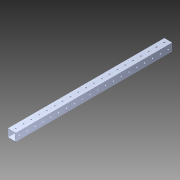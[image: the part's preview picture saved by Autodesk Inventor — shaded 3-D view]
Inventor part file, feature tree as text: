
AUTODESK INVENTOR PART (.ipt)
format: ipt  version: 2014 SP1 (Build 180222100, 222)  size: 1,191,936 bytes
history: native  units: in
note: dims shown in document units (in); Inventor stores cm internally (conversion verified against a paired STEP export)
features: pattern_circular x1, other x1, extrude x1, imported_body x1, sketch x1
ambient origin geometry x8: Origin, YZ Plane, XZ Plane, XY Plane, X Axis, Y Axis, Z Axis, Center Point
bodies: Body1 (feature_tree)
feature tree (5):
  pattern_circular  "CirPattern2"
  other  "1x1 tube1"
  extrude  "Extrusion1"  [1 undecoded]
  imported_body  "Base1"
  sketch  "Sketch1"  dims[d0=39.0in d1=0.0in]
note: 1 required parameter value undecoded (feature->parameter linkage not recoverable at this tier; creation-order binding heuristic only, values carry confidence <= 0.55)
